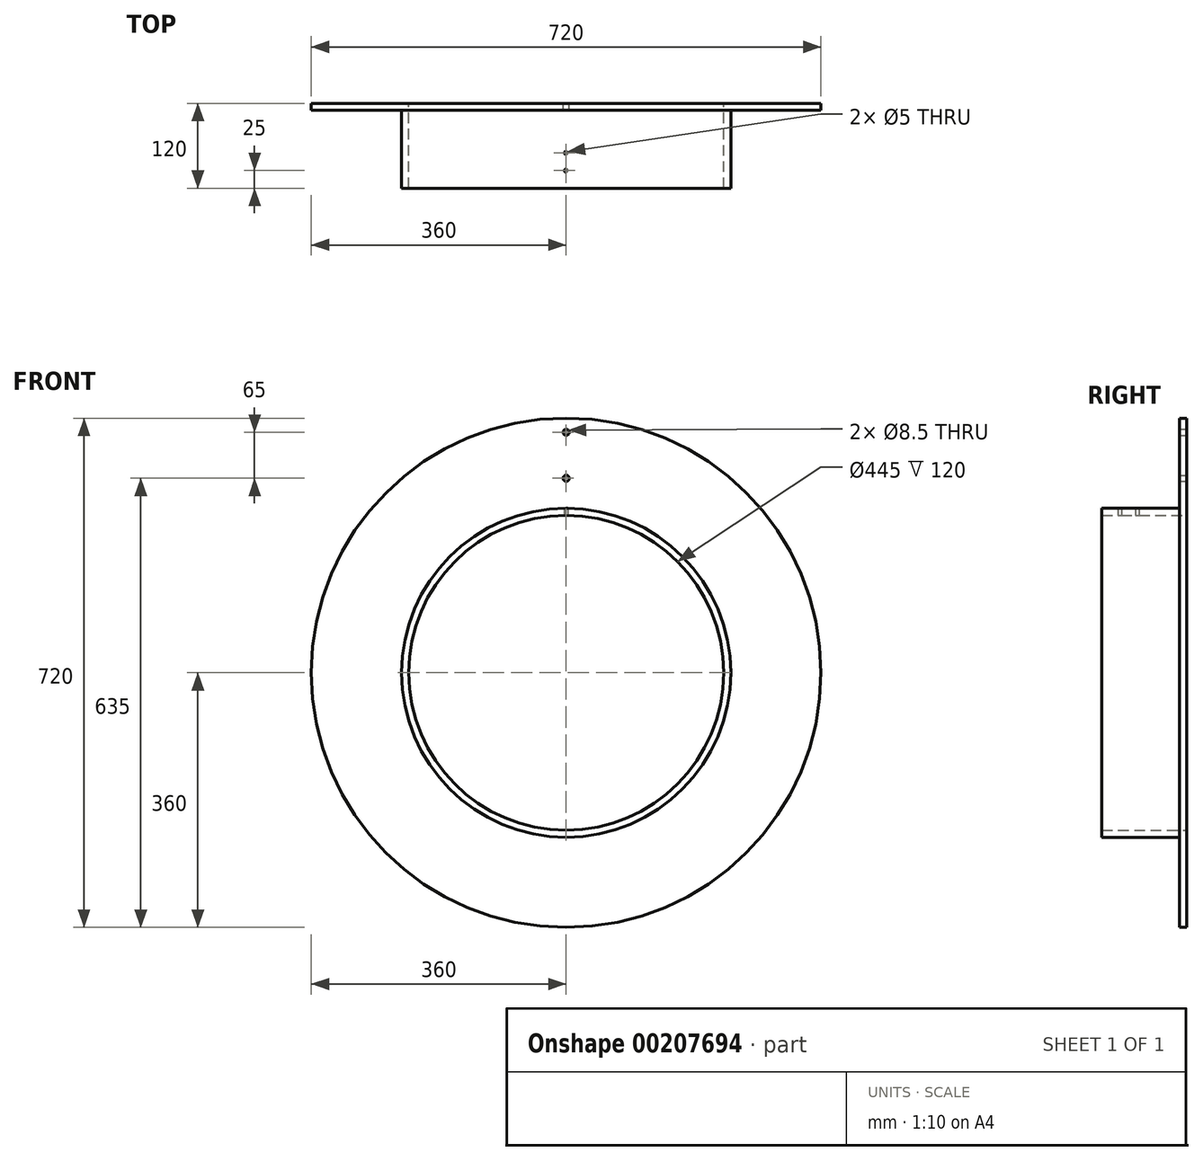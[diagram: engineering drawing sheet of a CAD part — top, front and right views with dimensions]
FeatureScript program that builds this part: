
annotation { "Feature Type Name" : "Feature", "Feature Type Description" : "" }
export const myFeature = defineFeature(function(context is Context, id is Id, definition is map)
    precondition{}
    {
        {
            var Q0;
            Q0=qCreatedBy(makeId("Front.planeOp"),FACE);
            var sketch = newSketch(context, id + "F0", { "sketchPlane" : qUnion([Q0])});
            skCircle(sketch, "E0", {"center": v(0, 0) * mm, "radius": 222.5 * mm});
            skCircle(sketch, "E1", {"center": v(0, 0) * mm, "radius": 232.5 * mm});
            skSolve(sketch);
        }
        {
            var Q0;
            Q0 = qSketchRegion(id + "F0", true);
            extrude(context, id + "F1", {"entities" : qUnion([Q0]), "endBound" : BoundingType.SYMMETRIC, "depth" : 120 * mm});
        }
        {
            var Q0;
            Q0=makeQuery(id+"F1.opExtrude","CAP_FACE",FACE,{"disambiguationData":[OSD([sQuery(id+"F0.wireOp",EDGE,"E0"),sQuery(id+"F0.wireOp",EDGE,"E1")])],"isStart":true});
            var sketch = newSketch(context, id + "F2", { "sketchPlane" : qUnion([Q0])});
            skCircle(sketch, "E2", {"center": v(0, 0) * mm, "radius": 360 * mm});
            skCircle(sketch, "E3", {"center": v(0, 0) * mm, "radius": 222.5 * mm});
            skSolve(sketch);
        }
        {
            var Q0;
            Q0=makeQuery(id+"F2.imprint","IMPRINT",FACE,{"disambiguationData":[TD([[makeQuery(id+"F2.imprint","IMPRINT",EDGE,{"derivedFrom":sQuery(id+"F2.wireOp",EDGE,"E2")}),1.0]])]});
            var Q1;
            Q1=makeQuery(id+"F2.imprint","IMPRINT",FACE,{"disambiguationData":[TD([[makeQuery(id+"F2.imprint","IMPRINT",EDGE,{"derivedFrom":sQuery(id+"F2.wireOp",EDGE,"E3")}),1.0]])]});
            extrude(context, id + "F3", {"entities" : qUnion([Q0, Q1]), "operationType" : NewBodyOperationType.ADD, "oppositeDirection" : true, "depth" : 10 * mm});
        }
        {
            var Q0;
            Q0=makeQuery(id+"F3.boolean.opBoolean","MERGE",FACE,{"derivedFrom":[makeQuery(id+"F1.opExtrude","CAP_FACE",FACE,{"disambiguationData":[OSD([sQuery(id+"F0.wireOp",EDGE,"E0"),sQuery(id+"F0.wireOp",EDGE,"E1")])],"isStart":true}),makeQuery(id+"F3.opExtrude","CAP_FACE",FACE,{"disambiguationData":[OSD([sQuery(id+"F2.wireOp",EDGE,"E2"),sQuery(id+"F2.wireOp",EDGE,"E3")])],"isStart":true})]});
            var sketch = newSketch(context, id + "F4", { "sketchPlane" : qUnion([Q0])});
            skCircle(sketch, "E4", {"center": v(0, 275) * mm, "radius": 5 * mm});
            skSolve(sketch);
        }
        {
            var Q0;
            Q0=sQuery(id+"F4.wireOp",VERTEX,"E4.center");
            var Q1;
            Q1=makeQuery(id+"F1.opExtrude","SWEPT_BODY",BODY,{"disambiguationData":[OSD([sQuery(id+"F0.wireOp",EDGE,"E0"),sQuery(id+"F0.wireOp",EDGE,"E1")])]});
            hole(context, id + "F5", {"style" : HoleStyle.SIMPLE, "endStyle" : HoleEndStyle.BLIND, "standardTappedOrClearance" : lookupTablePath({ "standard" : "ISO", "engagement" : "75%", "pitch" : "1.5 mm", "size" : "M10", "type" : "Tapped" }), "standardBlindInLast" : lookupTablePath({ "standard" : "ISO", "engagement" : "75%", "pitch" : "1.5 mm", "size" : "M10", "type" : "Tapped" }), "holeDiameter" : 8.5 * mm, "showTappedDepth" : true, "holeDepth" : 30 * mm, "tappedDepth" : 25.5 * mm, "tapClearance" : 3, "locations" : qUnion([Q0]), "scope" : qUnion([Q1]), "majorDiameter" : 10 * mm});
        }
        {
            var Q0;
            Q0=qCreatedBy(makeId("Top.planeOp"),FACE);
            var sketch = newSketch(context, id + "F6", { "sketchPlane" : qUnion([Q0])});
            skCircle(sketch, "E5", {"center": v(0, -35) * mm, "radius": 2.5 * mm});
            skCircle(sketch, "E6", {"center": v(0, -10) * mm, "radius": 2.5 * mm});
            skSolve(sketch);
        }
        {
            var Q0;
            Q0=makeQuery(id+"F6.imprint","IMPRINT",FACE,{"disambiguationData":[TD([[makeQuery(id+"F6.imprint","IMPRINT",EDGE,{"derivedFrom":sQuery(id+"F6.wireOp",EDGE,"E5")}),1.0]])]});
            var Q1;
            Q1=makeQuery(id+"F6.imprint","IMPRINT",FACE,{"disambiguationData":[TD([[makeQuery(id+"F6.imprint","IMPRINT",EDGE,{"derivedFrom":sQuery(id+"F6.wireOp",EDGE,"E6")}),1.0]])]});
            extrude(context, id + "F7", {"entities" : qUnion([Q0, Q1]), "operationType" : NewBodyOperationType.REMOVE, "depth" : 300 * mm});
        }
        {
            var Q0;
            Q0=makeQuery(id+"F3.boolean.opBoolean","MERGE",FACE,{"derivedFrom":[makeQuery(id+"F1.opExtrude","CAP_FACE",FACE,{"disambiguationData":[OSD([sQuery(id+"F0.wireOp",EDGE,"E0"),sQuery(id+"F0.wireOp",EDGE,"E1")])],"isStart":true}),makeQuery(id+"F3.opExtrude","CAP_FACE",FACE,{"disambiguationData":[OSD([sQuery(id+"F2.wireOp",EDGE,"E2"),sQuery(id+"F2.wireOp",EDGE,"E3")])],"isStart":true})]});
            var sketch = newSketch(context, id + "F8", { "sketchPlane" : qUnion([Q0])});
            skCircle(sketch, "E7", {"center": v(0, 340) * mm, "radius": 5 * mm});
            skSolve(sketch);
        }
        {
            var Q0;
            Q0=sQuery(id+"F8.wireOp",VERTEX,"E7.center");
            var Q1;
            Q1=makeQuery(id+"F1.opExtrude","SWEPT_BODY",BODY,{"disambiguationData":[OSD([sQuery(id+"F0.wireOp",EDGE,"E0"),sQuery(id+"F0.wireOp",EDGE,"E1")])]});
            hole(context, id + "F9", {"style" : HoleStyle.SIMPLE, "endStyle" : HoleEndStyle.BLIND, "standardTappedOrClearance" : lookupTablePath({ "standard" : "ISO", "engagement" : "75%", "pitch" : "1.5 mm", "size" : "M10", "type" : "Tapped" }), "standardBlindInLast" : lookupTablePath({ "standard" : "ISO", "engagement" : "75%", "pitch" : "1.5 mm", "size" : "M10", "type" : "Tapped" }), "holeDiameter" : 8.5 * mm, "showTappedDepth" : true, "holeDepth" : 22.1 * mm, "tappedDepth" : 17.6 * mm, "tapClearance" : 3, "locations" : qUnion([Q0]), "scope" : qUnion([Q1]), "majorDiameter" : 10 * mm});
        }
    });
